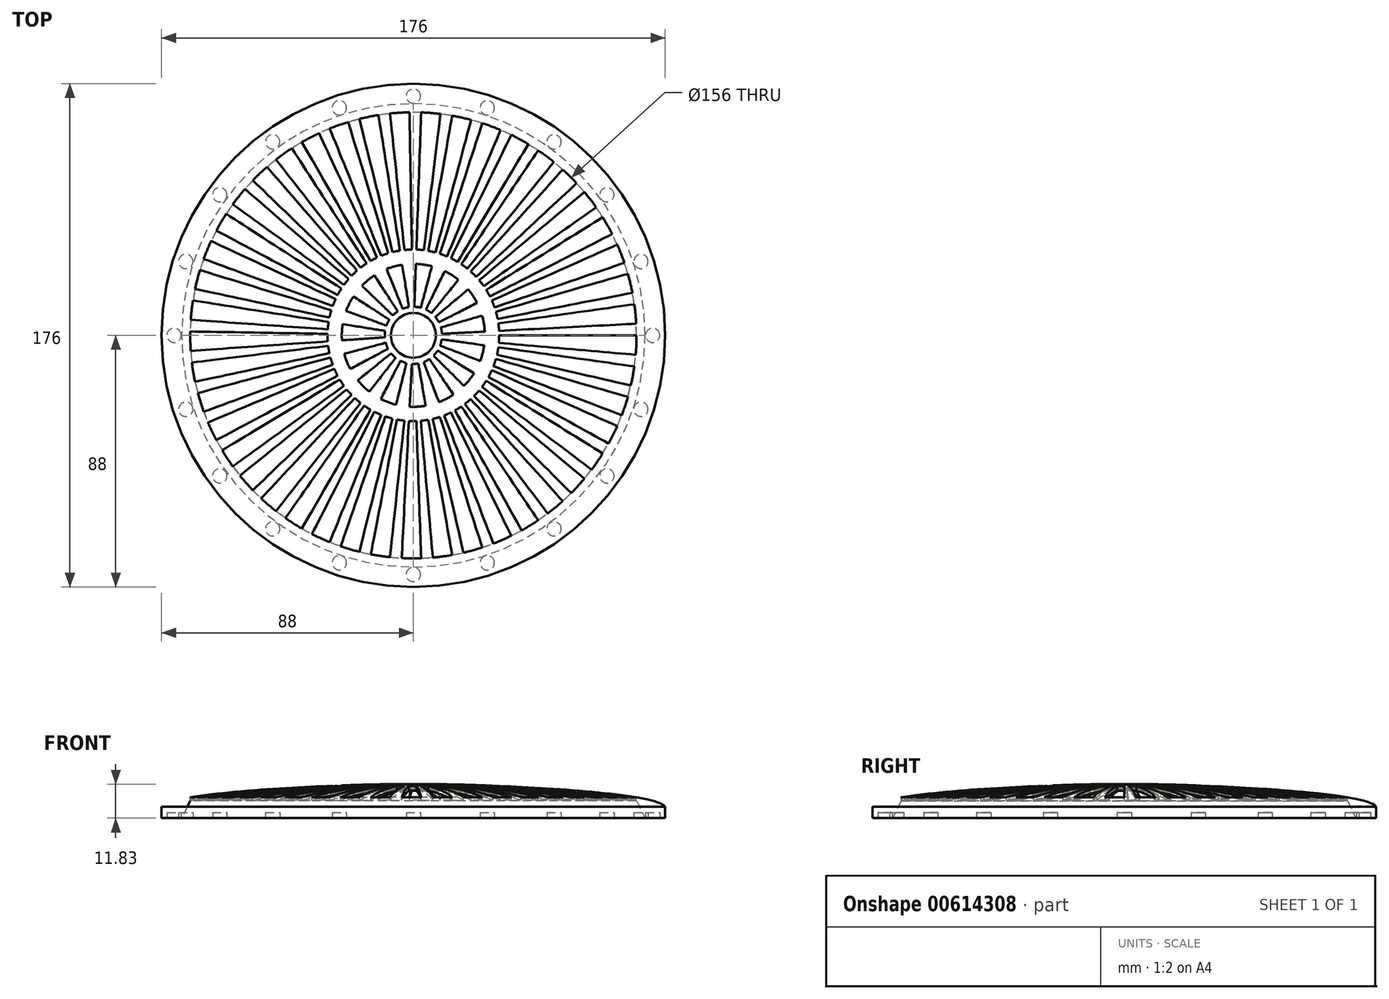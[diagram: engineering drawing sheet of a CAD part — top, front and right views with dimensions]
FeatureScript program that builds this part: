
annotation { "Feature Type Name" : "Feature", "Feature Type Description" : "" }
export const myFeature = defineFeature(function(context is Context, id is Id, definition is map)
    precondition{}
    {
        {
            var Q0;
            Q0=qCreatedBy(makeId("Right.planeOp"),FACE);
            var sketch = newSketch(context, id + "F0", { "sketchPlane" : qUnion([Q0])});
            skLineSegment(sketch, "E0", {"start": v(-78, 0) * mm, "end": v(-88, 0) * mm});
            skLineSegment(sketch, "E1", {"start": v(-88, 0) * mm, "end": v(-88, 4) * mm});
            skLineSegment(sketch, "E2", {"start": v(-88, 4) * mm, "end": v(-78, 4) * mm});
            skLineSegment(sketch, "E3", {"start": v(-78, 4) * mm, "end": v(-78, 0) * mm});
            skFitSpline(sketch, "E4", {"points": [v(-88, 4) * mm, v(-30.6, 11.2) * mm, v(0, 11.8) * mm], "startDerivative": vector(15.82, 21.77) * mm, "endDerivative": vector(56.9, -0.67) * mm});
            skFitSpline(sketch, "E5", {"points": [v(-86, 4) * mm, v(-30.52, 9.57) * mm, v(0, 10.3) * mm], "startDerivative": vector(13.53, 16.7) * mm, "endDerivative": vector(57.66, -2.55) * mm});
            skLineSegment(sketch, "E6", {"start": v(0, 11.8) * mm, "end": v(0, 10.3) * mm});
            skLineSegment(sketch, "E7", {"start": v(-78, 4) * mm, "end": v(-78, 6.25) * mm});
            skSolve(sketch);
        }
        {
            var Q0;
            Q0 = qSketchRegion(id + "F0", true);
            var Q1;
            Q1=sQuery(id+"F0.wireOp",EDGE,"E6");
            revolve(context, id + "F1", {"surfaceOperationType" : NewSurfaceOperationType.NEW, "entities" : qUnion([Q0]), "axis" : qUnion([Q1]), "revolveType" : RevolveType.FULL});
        }
        {
            var Q0;
            Q0=qCreatedBy(makeId("Top.planeOp"),FACE);
            var sketch = newSketch(context, id + "F2", { "sketchPlane" : qUnion([Q0])});
            skArc(sketch, "E8", {"start": v(78, 0) * mm, "mid": v(77.93, -3.4) * mm, "end": v(77.7, -6.8) * mm});
            skLineSegment(sketch, "E9", {"start": v(30, 0) * mm, "end": v(78, 0) * mm});
            skLineSegment(sketch, "E10", {"start": v(29.89, -2.61) * mm, "end": v(77.7, -6.8) * mm});
            skArc(sketch, "E11", {"start": v(30, 0) * mm, "mid": v(29.97, -1.3) * mm, "end": v(29.89, -2.61) * mm});
            skLineSegment(sketch, "E12.1.0", {"start": v(29.96, 1.57) * mm, "end": v(77.9, 4.08) * mm});
            skLineSegment(sketch, "E12.1.1", {"start": v(29.7, 4.18) * mm, "end": v(77.24, 10.86) * mm});
            skArc(sketch, "E12.1.2", {"start": v(77.24, 10.86) * mm, "mid": v(77.64, 7.48) * mm, "end": v(77.9, 4.08) * mm});
            skArc(sketch, "E12.1.3", {"start": v(29.7, 4.18) * mm, "mid": v(29.86, 2.88) * mm, "end": v(29.96, 1.57) * mm});
            skLineSegment(sketch, "E12.2.0", {"start": v(29.45, 5.72) * mm, "end": v(76.57, 14.88) * mm});
            skLineSegment(sketch, "E12.2.1", {"start": v(28.84, 8.27) * mm, "end": v(74.98, 21.5) * mm});
            skArc(sketch, "E12.2.2", {"start": v(74.98, 21.5) * mm, "mid": v(75.84, 18.2) * mm, "end": v(76.57, 14.88) * mm});
            skArc(sketch, "E12.2.3", {"start": v(28.84, 8.27) * mm, "mid": v(29.17, 7) * mm, "end": v(29.45, 5.72) * mm});
            skLineSegment(sketch, "E12.3.0", {"start": v(28.37, 9.77) * mm, "end": v(73.75, 25.4) * mm});
            skLineSegment(sketch, "E12.3.1", {"start": v(27.4, 12.2) * mm, "end": v(71.26, 31.73) * mm});
            skArc(sketch, "E12.3.2", {"start": v(71.26, 31.73) * mm, "mid": v(72.57, 28.59) * mm, "end": v(73.75, 25.4) * mm});
            skArc(sketch, "E12.3.3", {"start": v(27.4, 12.2) * mm, "mid": v(27.91, 11) * mm, "end": v(28.37, 9.77) * mm});
            skLineSegment(sketch, "E12.4.0", {"start": v(26.73, 13.62) * mm, "end": v(69.5, 35.41) * mm});
            skLineSegment(sketch, "E12.4.1", {"start": v(25.44, 15.9) * mm, "end": v(66.15, 41.33) * mm});
            skArc(sketch, "E12.4.2", {"start": v(66.15, 41.33) * mm, "mid": v(67.89, 38.4) * mm, "end": v(69.5, 35.41) * mm});
            skArc(sketch, "E12.4.3", {"start": v(25.44, 15.9) * mm, "mid": v(26.11, 14.77) * mm, "end": v(26.73, 13.62) * mm});
            skLineSegment(sketch, "E12.5.0", {"start": v(24.57, 17.2) * mm, "end": v(63.9, 44.74) * mm});
            skLineSegment(sketch, "E12.5.1", {"start": v(22.98, 19.28) * mm, "end": v(59.75, 50.14) * mm});
            skArc(sketch, "E12.5.2", {"start": v(59.75, 50.14) * mm, "mid": v(61.88, 47.48) * mm, "end": v(63.9, 44.74) * mm});
            skArc(sketch, "E12.5.3", {"start": v(22.98, 19.28) * mm, "mid": v(23.8, 18.26) * mm, "end": v(24.57, 17.2) * mm});
            skLineSegment(sketch, "E12.6.0", {"start": v(21.94, 20.46) * mm, "end": v(57.05, 53.2) * mm});
            skLineSegment(sketch, "E12.6.1", {"start": v(20.07, 22.3) * mm, "end": v(52.2, 57.97) * mm});
            skArc(sketch, "E12.6.2", {"start": v(52.2, 57.97) * mm, "mid": v(54.67, 55.63) * mm, "end": v(57.05, 53.2) * mm});
            skArc(sketch, "E12.6.3", {"start": v(20.07, 22.3) * mm, "mid": v(21.03, 21.4) * mm, "end": v(21.94, 20.46) * mm});
            skLineSegment(sketch, "E12.7.0", {"start": v(18.88, 23.31) * mm, "end": v(49.09, 60.62) * mm});
            skLineSegment(sketch, "E12.7.1", {"start": v(16.78, 24.87) * mm, "end": v(43.62, 64.66) * mm});
            skArc(sketch, "E12.7.2", {"start": v(43.62, 64.66) * mm, "mid": v(46.4, 62.7) * mm, "end": v(49.09, 60.62) * mm});
            skArc(sketch, "E12.7.3", {"start": v(16.78, 24.87) * mm, "mid": v(17.84, 24.12) * mm, "end": v(18.88, 23.31) * mm});
            skLineSegment(sketch, "E12.8.0", {"start": v(15.45, 25.72) * mm, "end": v(40.17, 66.86) * mm});
            skLineSegment(sketch, "E12.8.1", {"start": v(13.15, 26.96) * mm, "end": v(34.2, 70.1) * mm});
            skArc(sketch, "E12.8.2", {"start": v(34.2, 70.1) * mm, "mid": v(37.22, 68.55) * mm, "end": v(40.17, 66.86) * mm});
            skArc(sketch, "E12.8.3", {"start": v(13.15, 26.96) * mm, "mid": v(14.31, 26.36) * mm, "end": v(15.45, 25.72) * mm});
            skLineSegment(sketch, "E12.9.0", {"start": v(11.72, 27.62) * mm, "end": v(30.48, 71.8) * mm});
            skLineSegment(sketch, "E12.9.1", {"start": v(9.27, 28.53) * mm, "end": v(24.1, 74.18) * mm});
            skArc(sketch, "E12.9.2", {"start": v(24.1, 74.18) * mm, "mid": v(27.32, 73.06) * mm, "end": v(30.48, 71.8) * mm});
            skArc(sketch, "E12.9.3", {"start": v(9.27, 28.53) * mm, "mid": v(10.5, 28.1) * mm, "end": v(11.72, 27.62) * mm});
            skLineSegment(sketch, "E12.10.0", {"start": v(7.76, 28.98) * mm, "end": v(20.19, 75.34) * mm});
            skLineSegment(sketch, "E12.10.1", {"start": v(5.2, 29.54) * mm, "end": v(13.54, 76.82) * mm});
            skArc(sketch, "E12.10.2", {"start": v(13.54, 76.82) * mm, "mid": v(16.88, 76.15) * mm, "end": v(20.19, 75.34) * mm});
            skArc(sketch, "E12.10.3", {"start": v(5.2, 29.54) * mm, "mid": v(6.5, 29.29) * mm, "end": v(7.76, 28.98) * mm});
            skLineSegment(sketch, "E12.11.0", {"start": v(3.66, 29.78) * mm, "end": v(9.5, 77.42) * mm});
            skLineSegment(sketch, "E12.11.1", {"start": v(1.05, 29.98) * mm, "end": v(2.72, 77.95) * mm});
            skArc(sketch, "E12.11.2", {"start": v(2.72, 77.95) * mm, "mid": v(6.12, 77.76) * mm, "end": v(9.5, 77.42) * mm});
            skArc(sketch, "E12.11.3", {"start": v(1.05, 29.98) * mm, "mid": v(2.35, 29.9) * mm, "end": v(3.66, 29.78) * mm});
            skLineSegment(sketch, "E12.12.0", {"start": v(-0.52, 30) * mm, "end": v(-1.36, 77.99) * mm});
            skLineSegment(sketch, "E12.12.1", {"start": v(-3.14, 29.84) * mm, "end": v(-8.15, 77.57) * mm});
            skArc(sketch, "E12.12.2", {"start": v(-8.15, 77.57) * mm, "mid": v(-4.76, 77.85) * mm, "end": v(-1.36, 77.99) * mm});
            skArc(sketch, "E12.12.3", {"start": v(-3.14, 29.84) * mm, "mid": v(-1.83, 29.94) * mm, "end": v(-0.52, 30) * mm});
            skLineSegment(sketch, "E12.13.0", {"start": v(-4.7, 29.63) * mm, "end": v(-12.2, 77.04) * mm});
            skLineSegment(sketch, "E12.13.1", {"start": v(-7.26, 29.1) * mm, "end": v(-18.87, 75.68) * mm});
            skArc(sketch, "E12.13.2", {"start": v(-18.87, 75.68) * mm, "mid": v(-15.55, 76.43) * mm, "end": v(-12.2, 77.04) * mm});
            skArc(sketch, "E12.13.3", {"start": v(-7.26, 29.1) * mm, "mid": v(-5.98, 29.4) * mm, "end": v(-4.7, 29.63) * mm});
            skLineSegment(sketch, "E12.14.0", {"start": v(-8.77, 28.69) * mm, "end": v(-22.8, 74.6) * mm});
            skLineSegment(sketch, "E12.14.1", {"start": v(-11.24, 27.82) * mm, "end": v(-29.22, 72.32) * mm});
            skArc(sketch, "E12.14.2", {"start": v(-29.22, 72.32) * mm, "mid": v(-26.04, 73.53) * mm, "end": v(-22.8, 74.6) * mm});
            skArc(sketch, "E12.14.3", {"start": v(-11.24, 27.82) * mm, "mid": v(-10.01, 28.28) * mm, "end": v(-8.77, 28.69) * mm});
            skLineSegment(sketch, "E12.15.0", {"start": v(-12.68, 27.19) * mm, "end": v(-32.96, 70.7) * mm});
            skLineSegment(sketch, "E12.15.1", {"start": v(-15, 25.98) * mm, "end": v(-39, 67.55) * mm});
            skArc(sketch, "E12.15.2", {"start": v(-39, 67.55) * mm, "mid": v(-36.02, 69.19) * mm, "end": v(-32.96, 70.7) * mm});
            skArc(sketch, "E12.15.3", {"start": v(-15, 25.98) * mm, "mid": v(-13.85, 26.61) * mm, "end": v(-12.68, 27.19) * mm});
            skLineSegment(sketch, "E12.16.0", {"start": v(-16.34, 25.16) * mm, "end": v(-42.48, 65.42) * mm});
            skLineSegment(sketch, "E12.16.1", {"start": v(-18.47, 23.64) * mm, "end": v(-48.02, 61.46) * mm});
            skArc(sketch, "E12.16.2", {"start": v(-48.02, 61.46) * mm, "mid": v(-45.3, 63.5) * mm, "end": v(-42.48, 65.42) * mm});
            skArc(sketch, "E12.16.3", {"start": v(-18.47, 23.64) * mm, "mid": v(-17.42, 24.42) * mm, "end": v(-16.34, 25.16) * mm});
            skLineSegment(sketch, "E12.17.0", {"start": v(-19.68, 22.64) * mm, "end": v(-51.17, 58.87) * mm});
            skLineSegment(sketch, "E12.17.1", {"start": v(-21.58, 20.84) * mm, "end": v(-56.1, 54.18) * mm});
            skArc(sketch, "E12.17.2", {"start": v(-56.1, 54.18) * mm, "mid": v(-53.7, 56.58) * mm, "end": v(-51.17, 58.87) * mm});
            skArc(sketch, "E12.17.3", {"start": v(-21.58, 20.84) * mm, "mid": v(-20.65, 21.76) * mm, "end": v(-19.68, 22.64) * mm});
            skLineSegment(sketch, "E12.18.0", {"start": v(-22.64, 19.68) * mm, "end": v(-58.87, 51.17) * mm});
            skLineSegment(sketch, "E12.18.1", {"start": v(-24.27, 17.63) * mm, "end": v(-63.1, 45.85) * mm});
            skArc(sketch, "E12.18.2", {"start": v(-63.1, 45.85) * mm, "mid": v(-61.04, 48.56) * mm, "end": v(-58.87, 51.17) * mm});
            skArc(sketch, "E12.18.3", {"start": v(-24.27, 17.63) * mm, "mid": v(-23.48, 18.68) * mm, "end": v(-22.64, 19.68) * mm});
            skLineSegment(sketch, "E12.19.0", {"start": v(-25.16, 16.34) * mm, "end": v(-65.42, 42.48) * mm});
            skLineSegment(sketch, "E12.19.1", {"start": v(-26.49, 14.08) * mm, "end": v(-68.87, 36.62) * mm});
            skArc(sketch, "E12.19.2", {"start": v(-68.87, 36.62) * mm, "mid": v(-67.2, 39.59) * mm, "end": v(-65.42, 42.48) * mm});
            skArc(sketch, "E12.19.3", {"start": v(-26.49, 14.08) * mm, "mid": v(-25.85, 15.23) * mm, "end": v(-25.16, 16.34) * mm});
            skLineSegment(sketch, "E12.20.0", {"start": v(-27.19, 12.68) * mm, "end": v(-70.7, 32.96) * mm});
            skLineSegment(sketch, "E12.20.1", {"start": v(-28.2, 10.26) * mm, "end": v(-73.3, 26.68) * mm});
            skArc(sketch, "E12.20.2", {"start": v(-73.3, 26.68) * mm, "mid": v(-72.06, 29.85) * mm, "end": v(-70.7, 32.96) * mm});
            skArc(sketch, "E12.20.3", {"start": v(-28.2, 10.26) * mm, "mid": v(-27.72, 11.48) * mm, "end": v(-27.19, 12.68) * mm});
            skLineSegment(sketch, "E12.21.0", {"start": v(-28.69, 8.77) * mm, "end": v(-74.6, 22.8) * mm});
            skLineSegment(sketch, "E12.21.1", {"start": v(-29.34, 6.24) * mm, "end": v(-76.3, 16.22) * mm});
            skArc(sketch, "E12.21.2", {"start": v(-76.3, 16.22) * mm, "mid": v(-75.52, 19.53) * mm, "end": v(-74.6, 22.8) * mm});
            skArc(sketch, "E12.21.3", {"start": v(-29.34, 6.24) * mm, "mid": v(-29.04, 7.51) * mm, "end": v(-28.69, 8.77) * mm});
            skLineSegment(sketch, "E12.22.0", {"start": v(-29.63, 4.7) * mm, "end": v(-77.04, 12.2) * mm});
            skLineSegment(sketch, "E12.22.1", {"start": v(-29.93, 2.1) * mm, "end": v(-77.8, 5.44) * mm});
            skArc(sketch, "E12.22.2", {"start": v(-77.8, 5.44) * mm, "mid": v(-77.5, 8.83) * mm, "end": v(-77.04, 12.2) * mm});
            skArc(sketch, "E12.22.3", {"start": v(-29.93, 2.1) * mm, "mid": v(-29.8, 3.4) * mm, "end": v(-29.63, 4.7) * mm});
            skLineSegment(sketch, "E12.23.0", {"start": v(-30, 0.52) * mm, "end": v(-77.99, 1.36) * mm});
            skLineSegment(sketch, "E12.23.1", {"start": v(-29.93, -2.1) * mm, "end": v(-77.8, -5.44) * mm});
            skArc(sketch, "E12.23.2", {"start": v(-77.8, -5.44) * mm, "mid": v(-77.97, -2.04) * mm, "end": v(-77.99, 1.36) * mm});
            skArc(sketch, "E12.23.3", {"start": v(-29.93, -2.1) * mm, "mid": v(-29.99, -0.79) * mm, "end": v(-30, 0.52) * mm});
            skLineSegment(sketch, "E12.24.0", {"start": v(-29.78, -3.66) * mm, "end": v(-77.42, -9.5) * mm});
            skLineSegment(sketch, "E12.24.1", {"start": v(-29.34, -6.24) * mm, "end": v(-76.3, -16.22) * mm});
            skArc(sketch, "E12.24.2", {"start": v(-76.3, -16.22) * mm, "mid": v(-76.93, -12.87) * mm, "end": v(-77.42, -9.5) * mm});
            skArc(sketch, "E12.24.3", {"start": v(-29.34, -6.24) * mm, "mid": v(-29.59, -4.95) * mm, "end": v(-29.78, -3.66) * mm});
            skLineSegment(sketch, "E12.25.0", {"start": v(-28.98, -7.76) * mm, "end": v(-75.34, -20.19) * mm});
            skLineSegment(sketch, "E12.25.1", {"start": v(-28.2, -10.26) * mm, "end": v(-73.3, -26.68) * mm});
            skArc(sketch, "E12.25.2", {"start": v(-73.3, -26.68) * mm, "mid": v(-74.39, -23.46) * mm, "end": v(-75.34, -20.19) * mm});
            skArc(sketch, "E12.25.3", {"start": v(-28.2, -10.26) * mm, "mid": v(-28.61, -9.02) * mm, "end": v(-28.98, -7.76) * mm});
            skLineSegment(sketch, "E12.26.0", {"start": v(-27.62, -11.72) * mm, "end": v(-71.8, -30.48) * mm});
            skLineSegment(sketch, "E12.26.1", {"start": v(-26.49, -14.08) * mm, "end": v(-68.87, -36.62) * mm});
            skArc(sketch, "E12.26.2", {"start": v(-68.87, -36.62) * mm, "mid": v(-70.4, -33.58) * mm, "end": v(-71.8, -30.48) * mm});
            skArc(sketch, "E12.26.3", {"start": v(-26.49, -14.08) * mm, "mid": v(-27.08, -12.92) * mm, "end": v(-27.62, -11.72) * mm});
            skLineSegment(sketch, "E12.27.0", {"start": v(-25.72, -15.45) * mm, "end": v(-66.86, -40.17) * mm});
            skLineSegment(sketch, "E12.27.1", {"start": v(-24.27, -17.63) * mm, "end": v(-63.1, -45.85) * mm});
            skArc(sketch, "E12.27.2", {"start": v(-63.1, -45.85) * mm, "mid": v(-65.04, -43.05) * mm, "end": v(-66.86, -40.17) * mm});
            skArc(sketch, "E12.27.3", {"start": v(-24.27, -17.63) * mm, "mid": v(-25.02, -16.56) * mm, "end": v(-25.72, -15.45) * mm});
            skLineSegment(sketch, "E12.28.0", {"start": v(-23.31, -18.88) * mm, "end": v(-60.62, -49.09) * mm});
            skLineSegment(sketch, "E12.28.1", {"start": v(-21.58, -20.84) * mm, "end": v(-56.1, -54.18) * mm});
            skArc(sketch, "E12.28.2", {"start": v(-56.1, -54.18) * mm, "mid": v(-58.42, -51.68) * mm, "end": v(-60.62, -49.09) * mm});
            skArc(sketch, "E12.28.3", {"start": v(-21.58, -20.84) * mm, "mid": v(-22.47, -19.88) * mm, "end": v(-23.31, -18.88) * mm});
            skLineSegment(sketch, "E12.29.0", {"start": v(-20.46, -21.94) * mm, "end": v(-53.2, -57.05) * mm});
            skLineSegment(sketch, "E12.29.1", {"start": v(-18.47, -23.64) * mm, "end": v(-48.02, -61.46) * mm});
            skArc(sketch, "E12.29.2", {"start": v(-48.02, -61.46) * mm, "mid": v(-50.66, -59.31) * mm, "end": v(-53.2, -57.05) * mm});
            skArc(sketch, "E12.29.3", {"start": v(-18.47, -23.64) * mm, "mid": v(-19.48, -22.81) * mm, "end": v(-20.46, -21.94) * mm});
            skLineSegment(sketch, "E13.1.30.0", {"start": v(-17.2, -24.57) * mm, "end": v(-44.74, -63.9) * mm});
            skLineSegment(sketch, "E13.3.30.0", {"start": v(-15, -25.98) * mm, "end": v(-39, -67.55) * mm});
            skArc(sketch, "E13.6.30.0", {"start": v(-39, -67.55) * mm, "mid": v(-41.9, -65.78) * mm, "end": v(-44.74, -63.9) * mm});
            skArc(sketch, "E13.10.30.0", {"start": v(-15, -25.98) * mm, "mid": v(-16.12, -25.3) * mm, "end": v(-17.2, -24.57) * mm});
            skLineSegment(sketch, "E13.1.31.0", {"start": v(-13.62, -26.73) * mm, "end": v(-35.41, -69.5) * mm});
            skLineSegment(sketch, "E13.3.31.0", {"start": v(-11.24, -27.82) * mm, "end": v(-29.22, -72.32) * mm});
            skArc(sketch, "E13.6.31.0", {"start": v(-29.22, -72.32) * mm, "mid": v(-32.35, -70.98) * mm, "end": v(-35.41, -69.5) * mm});
            skArc(sketch, "E13.10.31.0", {"start": v(-11.24, -27.82) * mm, "mid": v(-12.44, -27.3) * mm, "end": v(-13.62, -26.73) * mm});
            skLineSegment(sketch, "E13.1.32.0", {"start": v(-9.77, -28.37) * mm, "end": v(-25.4, -73.75) * mm});
            skLineSegment(sketch, "E13.3.32.0", {"start": v(-7.26, -29.1) * mm, "end": v(-18.87, -75.68) * mm});
            skArc(sketch, "E13.6.32.0", {"start": v(-18.87, -75.68) * mm, "mid": v(-22.15, -74.79) * mm, "end": v(-25.4, -73.75) * mm});
            skArc(sketch, "E13.10.32.0", {"start": v(-7.26, -29.1) * mm, "mid": v(-8.52, -28.76) * mm, "end": v(-9.77, -28.37) * mm});
            skLineSegment(sketch, "E13.1.33.0", {"start": v(-5.72, -29.45) * mm, "end": v(-14.88, -76.57) * mm});
            skLineSegment(sketch, "E13.3.33.0", {"start": v(-3.14, -29.84) * mm, "end": v(-8.15, -77.57) * mm});
            skArc(sketch, "E13.6.33.0", {"start": v(-8.15, -77.57) * mm, "mid": v(-11.53, -77.14) * mm, "end": v(-14.88, -76.57) * mm});
            skArc(sketch, "E13.10.33.0", {"start": v(-3.14, -29.84) * mm, "mid": v(-4.43, -29.67) * mm, "end": v(-5.72, -29.45) * mm});
            skLineSegment(sketch, "E13.1.34.0", {"start": v(-1.57, -29.96) * mm, "end": v(-4.08, -77.9) * mm});
            skLineSegment(sketch, "E13.3.34.0", {"start": v(1.05, -29.98) * mm, "end": v(2.72, -77.95) * mm});
            skArc(sketch, "E13.6.34.0", {"start": v(2.72, -77.95) * mm, "mid": v(-0.68, -78) * mm, "end": v(-4.08, -77.9) * mm});
            skArc(sketch, "E13.10.34.0", {"start": v(1.05, -29.98) * mm, "mid": v(-0.26, -30) * mm, "end": v(-1.57, -29.96) * mm});
            skLineSegment(sketch, "E13.1.35.0", {"start": v(2.61, -29.89) * mm, "end": v(6.8, -77.7) * mm});
            skLineSegment(sketch, "E13.3.35.0", {"start": v(5.2, -29.54) * mm, "end": v(13.54, -76.82) * mm});
            skArc(sketch, "E13.6.35.0", {"start": v(13.54, -76.82) * mm, "mid": v(10.18, -77.33) * mm, "end": v(6.8, -77.7) * mm});
            skArc(sketch, "E13.10.35.0", {"start": v(5.2, -29.54) * mm, "mid": v(3.92, -29.74) * mm, "end": v(2.61, -29.89) * mm});
            skLineSegment(sketch, "E13.1.36.0", {"start": v(6.75, -29.23) * mm, "end": v(17.55, -76) * mm});
            skLineSegment(sketch, "E13.3.36.0", {"start": v(9.27, -28.53) * mm, "end": v(24.1, -74.18) * mm});
            skArc(sketch, "E13.6.36.0", {"start": v(24.1, -74.18) * mm, "mid": v(20.84, -75.16) * mm, "end": v(17.55, -76) * mm});
            skArc(sketch, "E13.10.36.0", {"start": v(9.27, -28.53) * mm, "mid": v(8.02, -28.9) * mm, "end": v(6.75, -29.23) * mm});
            skLineSegment(sketch, "E13.1.37.0", {"start": v(10.75, -28) * mm, "end": v(27.95, -72.82) * mm});
            skLineSegment(sketch, "E13.3.37.0", {"start": v(13.15, -26.96) * mm, "end": v(34.2, -70.1) * mm});
            skArc(sketch, "E13.6.37.0", {"start": v(34.2, -70.1) * mm, "mid": v(31.1, -71.53) * mm, "end": v(27.95, -72.82) * mm});
            skArc(sketch, "E13.10.37.0", {"start": v(13.15, -26.96) * mm, "mid": v(11.96, -27.51) * mm, "end": v(10.75, -28) * mm});
            skLineSegment(sketch, "E13.1.38.0", {"start": v(14.54, -26.24) * mm, "end": v(37.82, -68.22) * mm});
            skLineSegment(sketch, "E13.3.38.0", {"start": v(16.78, -24.87) * mm, "end": v(43.62, -64.66) * mm});
            skArc(sketch, "E13.6.38.0", {"start": v(43.62, -64.66) * mm, "mid": v(40.75, -66.5) * mm, "end": v(37.82, -68.22) * mm});
            skArc(sketch, "E13.10.38.0", {"start": v(16.78, -24.87) * mm, "mid": v(15.67, -25.58) * mm, "end": v(14.54, -26.24) * mm});
            skLineSegment(sketch, "E13.1.39.0", {"start": v(18.05, -23.96) * mm, "end": v(46.94, -62.3) * mm});
            skLineSegment(sketch, "E13.3.39.0", {"start": v(20.07, -22.3) * mm, "end": v(52.2, -57.97) * mm});
            skArc(sketch, "E13.6.39.0", {"start": v(52.2, -57.97) * mm, "mid": v(49.61, -60.19) * mm, "end": v(46.94, -62.3) * mm});
            skArc(sketch, "E13.10.39.0", {"start": v(20.07, -22.3) * mm, "mid": v(19.08, -23.15) * mm, "end": v(18.05, -23.96) * mm});
            skLineSegment(sketch, "E13.1.40.0", {"start": v(21.21, -21.21) * mm, "end": v(55.15, -55.15) * mm});
            skLineSegment(sketch, "E13.3.40.0", {"start": v(22.98, -19.28) * mm, "end": v(59.75, -50.14) * mm});
            skArc(sketch, "E13.6.40.0", {"start": v(59.75, -50.14) * mm, "mid": v(57.5, -52.7) * mm, "end": v(55.15, -55.15) * mm});
            skArc(sketch, "E13.10.40.0", {"start": v(22.98, -19.28) * mm, "mid": v(22.12, -20.27) * mm, "end": v(21.21, -21.21) * mm});
            skLineSegment(sketch, "E13.1.41.0", {"start": v(23.96, -18.05) * mm, "end": v(62.3, -46.94) * mm});
            skLineSegment(sketch, "E13.3.41.0", {"start": v(25.44, -15.9) * mm, "end": v(66.15, -41.33) * mm});
            skArc(sketch, "E13.6.41.0", {"start": v(66.15, -41.33) * mm, "mid": v(64.28, -44.18) * mm, "end": v(62.3, -46.94) * mm});
            skArc(sketch, "E13.10.41.0", {"start": v(25.44, -15.9) * mm, "mid": v(24.72, -17) * mm, "end": v(23.96, -18.05) * mm});
            skLineSegment(sketch, "E13.1.42.0", {"start": v(26.24, -14.54) * mm, "end": v(68.22, -37.82) * mm});
            skLineSegment(sketch, "E13.3.42.0", {"start": v(27.4, -12.2) * mm, "end": v(71.26, -31.73) * mm});
            skArc(sketch, "E13.6.42.0", {"start": v(71.26, -31.73) * mm, "mid": v(69.8, -34.8) * mm, "end": v(68.22, -37.82) * mm});
            skArc(sketch, "E13.10.42.0", {"start": v(27.4, -12.2) * mm, "mid": v(26.85, -13.39) * mm, "end": v(26.24, -14.54) * mm});
            skLineSegment(sketch, "E13.1.43.0", {"start": v(28, -10.75) * mm, "end": v(72.82, -27.95) * mm});
            skLineSegment(sketch, "E13.3.43.0", {"start": v(28.84, -8.27) * mm, "end": v(74.98, -21.5) * mm});
            skArc(sketch, "E13.6.43.0", {"start": v(74.98, -21.5) * mm, "mid": v(73.97, -24.75) * mm, "end": v(72.82, -27.95) * mm});
            skArc(sketch, "E13.10.43.0", {"start": v(28.84, -8.27) * mm, "mid": v(28.45, -9.52) * mm, "end": v(28, -10.75) * mm});
            skLineSegment(sketch, "E13.1.44.0", {"start": v(29.23, -6.75) * mm, "end": v(76, -17.55) * mm});
            skLineSegment(sketch, "E13.3.44.0", {"start": v(29.7, -4.18) * mm, "end": v(77.24, -10.86) * mm});
            skArc(sketch, "E13.6.44.0", {"start": v(77.24, -10.86) * mm, "mid": v(76.7, -14.21) * mm, "end": v(76, -17.55) * mm});
            skArc(sketch, "E13.10.44.0", {"start": v(29.7, -4.18) * mm, "mid": v(29.5, -5.47) * mm, "end": v(29.23, -6.75) * mm});
            skArc(sketch, "E14", {"start": v(-24.7, 3.91) * mm, "mid": v(-24.98, 1.1) * mm, "end": v(-24.94, -1.74) * mm});
            skLineSegment(sketch, "E15", {"start": v(-9.88, 1.56) * mm, "end": v(-24.7, 3.91) * mm});
            skLineSegment(sketch, "E16", {"start": v(-9.98, -0.7) * mm, "end": v(-24.94, -1.74) * mm});
            skCircle(sketch, "E17", {"center": v(0, 0) * mm, "radius": 7.85 * mm});
            skArc(sketch, "E18", {"start": v(-9.98, -0.7) * mm, "mid": v(-10, 0.44) * mm, "end": v(-9.88, 1.56) * mm});
            skLineSegment(sketch, "E19.1.0", {"start": v(-9.66, -2.59) * mm, "end": v(-24.15, -6.47) * mm});
            skArc(sketch, "E19.1.1", {"start": v(-24.15, -6.47) * mm, "mid": v(-23.26, -9.16) * mm, "end": v(-22.07, -11.74) * mm});
            skLineSegment(sketch, "E19.1.2", {"start": v(-8.83, -4.7) * mm, "end": v(-22.07, -11.74) * mm});
            skArc(sketch, "E19.1.3", {"start": v(-8.83, -4.7) * mm, "mid": v(-9.3, -3.67) * mm, "end": v(-9.66, -2.59) * mm});
            skLineSegment(sketch, "E19.2.0", {"start": v(-7.77, -6.3) * mm, "end": v(-19.43, -15.73) * mm});
            skArc(sketch, "E19.2.1", {"start": v(-19.43, -15.73) * mm, "mid": v(-17.52, -17.83) * mm, "end": v(-15.4, -19.7) * mm});
            skLineSegment(sketch, "E19.2.2", {"start": v(-6.16, -7.88) * mm, "end": v(-15.4, -19.7) * mm});
            skArc(sketch, "E19.2.3", {"start": v(-6.16, -7.88) * mm, "mid": v(-7, -7.13) * mm, "end": v(-7.77, -6.3) * mm});
            skLineSegment(sketch, "E19.3.0", {"start": v(-4.54, -8.91) * mm, "end": v(-11.35, -22.28) * mm});
            skArc(sketch, "E19.3.1", {"start": v(-11.35, -22.28) * mm, "mid": v(-8.76, -23.42) * mm, "end": v(-6.05, -24.26) * mm});
            skLineSegment(sketch, "E19.3.2", {"start": v(-2.42, -9.7) * mm, "end": v(-6.05, -24.26) * mm});
            skArc(sketch, "E19.3.3", {"start": v(-2.42, -9.7) * mm, "mid": v(-3.5, -9.37) * mm, "end": v(-4.54, -8.91) * mm});
            skLineSegment(sketch, "E19.4.0", {"start": v(-0.52, -9.99) * mm, "end": v(-1.3, -24.97) * mm});
            skArc(sketch, "E19.4.1", {"start": v(-1.3, -24.97) * mm, "mid": v(1.53, -24.95) * mm, "end": v(4.34, -24.62) * mm});
            skLineSegment(sketch, "E19.4.2", {"start": v(1.74, -9.85) * mm, "end": v(4.34, -24.62) * mm});
            skArc(sketch, "E19.4.3", {"start": v(1.74, -9.85) * mm, "mid": v(0.61, -9.98) * mm, "end": v(-0.52, -9.99) * mm});
            skLineSegment(sketch, "E19.5.0", {"start": v(3.58, -9.34) * mm, "end": v(8.96, -23.34) * mm});
            skArc(sketch, "E19.5.1", {"start": v(8.96, -23.34) * mm, "mid": v(11.54, -22.18) * mm, "end": v(13.98, -20.73) * mm});
            skLineSegment(sketch, "E19.5.2", {"start": v(5.6, -8.3) * mm, "end": v(13.98, -20.73) * mm});
            skArc(sketch, "E19.5.3", {"start": v(5.6, -8.3) * mm, "mid": v(4.62, -8.87) * mm, "end": v(3.58, -9.34) * mm});
            skLineSegment(sketch, "E19.6.0", {"start": v(7.07, -7.07) * mm, "end": v(17.68, -17.68) * mm});
            skArc(sketch, "E19.6.1", {"start": v(17.68, -17.68) * mm, "mid": v(19.57, -15.56) * mm, "end": v(21.2, -13.25) * mm});
            skLineSegment(sketch, "E19.6.2", {"start": v(8.48, -5.3) * mm, "end": v(21.2, -13.25) * mm});
            skArc(sketch, "E19.6.3", {"start": v(8.48, -5.3) * mm, "mid": v(7.83, -6.23) * mm, "end": v(7.07, -7.07) * mm});
            skLineSegment(sketch, "E19.7.0", {"start": v(9.34, -3.58) * mm, "end": v(23.34, -8.96) * mm});
            skArc(sketch, "E19.7.1", {"start": v(23.34, -8.96) * mm, "mid": v(24.2, -6.26) * mm, "end": v(24.76, -3.48) * mm});
            skLineSegment(sketch, "E19.7.2", {"start": v(9.9, -1.4) * mm, "end": v(24.76, -3.48) * mm});
            skArc(sketch, "E19.7.3", {"start": v(9.9, -1.4) * mm, "mid": v(9.68, -2.5) * mm, "end": v(9.34, -3.58) * mm});
            skLineSegment(sketch, "E19.8.0", {"start": v(9.99, 0.52) * mm, "end": v(24.97, 1.3) * mm});
            skArc(sketch, "E19.8.1", {"start": v(24.97, 1.3) * mm, "mid": v(24.66, 4.13) * mm, "end": v(24.03, 6.9) * mm});
            skLineSegment(sketch, "E19.8.2", {"start": v(9.61, 2.76) * mm, "end": v(24.03, 6.9) * mm});
            skArc(sketch, "E19.8.3", {"start": v(9.61, 2.76) * mm, "mid": v(9.86, 1.65) * mm, "end": v(9.99, 0.52) * mm});
            skLineSegment(sketch, "E19.9.0", {"start": v(8.91, 4.54) * mm, "end": v(22.28, 11.35) * mm});
            skArc(sketch, "E19.9.1", {"start": v(22.28, 11.35) * mm, "mid": v(20.85, 13.8) * mm, "end": v(19.15, 16.07) * mm});
            skLineSegment(sketch, "E19.9.2", {"start": v(7.66, 6.43) * mm, "end": v(19.15, 16.07) * mm});
            skArc(sketch, "E19.9.3", {"start": v(7.66, 6.43) * mm, "mid": v(8.34, 5.52) * mm, "end": v(8.91, 4.54) * mm});
            skLineSegment(sketch, "E19.10.0", {"start": v(6.3, 7.77) * mm, "end": v(15.73, 19.43) * mm});
            skArc(sketch, "E19.10.1", {"start": v(15.73, 19.43) * mm, "mid": v(13.43, 21.08) * mm, "end": v(10.96, 22.47) * mm});
            skLineSegment(sketch, "E19.10.2", {"start": v(4.38, 8.99) * mm, "end": v(10.96, 22.47) * mm});
            skArc(sketch, "E19.10.3", {"start": v(4.38, 8.99) * mm, "mid": v(5.37, 8.43) * mm, "end": v(6.3, 7.77) * mm});
            skLineSegment(sketch, "E19.11.0", {"start": v(2.59, 9.66) * mm, "end": v(6.47, 24.15) * mm});
            skArc(sketch, "E19.11.1", {"start": v(6.47, 24.15) * mm, "mid": v(3.7, 24.73) * mm, "end": v(0.87, 24.98) * mm});
            skLineSegment(sketch, "E19.11.2", {"start": v(0.35, 10) * mm, "end": v(0.87, 24.98) * mm});
            skArc(sketch, "E19.11.3", {"start": v(0.35, 10) * mm, "mid": v(1.48, 9.9) * mm, "end": v(2.59, 9.66) * mm});
            skLineSegment(sketch, "E19.12.0", {"start": v(-1.56, 9.88) * mm, "end": v(-3.91, 24.7) * mm});
            skArc(sketch, "E19.12.1", {"start": v(-3.91, 24.7) * mm, "mid": v(-6.68, 24.1) * mm, "end": v(-9.37, 23.18) * mm});
            skLineSegment(sketch, "E19.12.2", {"start": v(-3.75, 9.27) * mm, "end": v(-9.37, 23.18) * mm});
            skArc(sketch, "E19.12.3", {"start": v(-3.75, 9.27) * mm, "mid": v(-2.67, 9.64) * mm, "end": v(-1.56, 9.88) * mm});
            skLineSegment(sketch, "E19.13.0", {"start": v(-5.45, 8.39) * mm, "end": v(-13.62, 20.97) * mm});
            skArc(sketch, "E19.13.1", {"start": v(-13.62, 20.97) * mm, "mid": v(-15.9, 19.3) * mm, "end": v(-17.98, 17.37) * mm});
            skLineSegment(sketch, "E19.13.2", {"start": v(-7.2, 6.95) * mm, "end": v(-17.98, 17.37) * mm});
            skArc(sketch, "E19.13.3", {"start": v(-7.2, 6.95) * mm, "mid": v(-6.36, 7.72) * mm, "end": v(-5.45, 8.39) * mm});
            skLineSegment(sketch, "E19.14.0", {"start": v(-8.39, 5.45) * mm, "end": v(-20.97, 13.62) * mm});
            skArc(sketch, "E19.14.1", {"start": v(-20.97, 13.62) * mm, "mid": v(-22.37, 11.15) * mm, "end": v(-23.5, 8.55) * mm});
            skLineSegment(sketch, "E19.14.2", {"start": v(-9.4, 3.42) * mm, "end": v(-23.5, 8.55) * mm});
            skArc(sketch, "E19.14.3", {"start": v(-9.4, 3.42) * mm, "mid": v(-8.95, 4.46) * mm, "end": v(-8.39, 5.45) * mm});
            skSolve(sketch);
        }
        {
            var Q0;
            Q0 = qSketchRegion(id + "F2", true);
            var Q1;
            Q1=makeQuery(id+"F1.opRevolve","SWEPT_BODY",BODY,{"disambiguationData":[OSD([sQuery(id+"F0.wireOp",EDGE,"E0"),sQuery(id+"F0.wireOp",EDGE,"E1"),sQuery(id+"F0.wireOp",EDGE,"E2"),sQuery(id+"F0.wireOp",EDGE,"E3"),sQuery(id+"F0.wireOp",EDGE,"E4"),sQuery(id+"F0.wireOp",EDGE,"E5"),sQuery(id+"F0.wireOp",EDGE,"E6")])]});
            extrude(context, id + "F3", {"entities" : qUnion([Q0]), "operationType" : NewBodyOperationType.REMOVE, "oppositeDirection" : true, "depth" : 25 * mm, "endBoundEntityBody" : qUnion([Q1]), "offsetDistance" : 25 * mm, "hasSecondDirection" : true, "secondDirectionOppositeDirection" : false, "secondDirectionDepth" : 26.4 * mm});
        }
        {
            var Q0;
            Q0=makeQuery(id+"F1.opRevolve","SWEPT_FACE",FACE,{"disambiguationData":[OSD([sQuery(id+"F0.wireOp",EDGE,"E0")])]});
            var sketch = newSketch(context, id + "F4", { "sketchPlane" : qUnion([Q0])});
            skCircle(sketch, "E20", {"center": v(0, -83.65) * mm, "radius": 2.5 * mm});
            skCircle(sketch, "E21.1.0", {"center": v(25.85, -79.55) * mm, "radius": 2.5 * mm});
            skCircle(sketch, "E21.2.0", {"center": v(49.17, -67.67) * mm, "radius": 2.5 * mm});
            skCircle(sketch, "E21.3.0", {"center": v(67.67, -49.17) * mm, "radius": 2.5 * mm});
            skCircle(sketch, "E21.4.0", {"center": v(79.55, -25.85) * mm, "radius": 2.5 * mm});
            skCircle(sketch, "E21.5.0", {"center": v(83.65, 0) * mm, "radius": 2.5 * mm});
            skCircle(sketch, "E21.6.0", {"center": v(79.55, 25.85) * mm, "radius": 2.5 * mm});
            skCircle(sketch, "E21.7.0", {"center": v(67.67, 49.17) * mm, "radius": 2.5 * mm});
            skCircle(sketch, "E21.8.0", {"center": v(49.17, 67.67) * mm, "radius": 2.5 * mm});
            skCircle(sketch, "E21.9.0", {"center": v(25.85, 79.55) * mm, "radius": 2.5 * mm});
            skCircle(sketch, "E21.10.0", {"center": v(0, 83.65) * mm, "radius": 2.5 * mm});
            skCircle(sketch, "E21.11.0", {"center": v(-25.85, 79.55) * mm, "radius": 2.5 * mm});
            skCircle(sketch, "E21.12.0", {"center": v(-49.17, 67.67) * mm, "radius": 2.5 * mm});
            skCircle(sketch, "E21.13.0", {"center": v(-67.67, 49.17) * mm, "radius": 2.5 * mm});
            skCircle(sketch, "E21.14.0", {"center": v(-79.55, 25.85) * mm, "radius": 2.5 * mm});
            skCircle(sketch, "E21.15.0", {"center": v(-83.65, 0) * mm, "radius": 2.5 * mm});
            skCircle(sketch, "E21.16.0", {"center": v(-79.55, -25.85) * mm, "radius": 2.5 * mm});
            skCircle(sketch, "E21.17.0", {"center": v(-67.67, -49.17) * mm, "radius": 2.5 * mm});
            skCircle(sketch, "E21.18.0", {"center": v(-49.17, -67.67) * mm, "radius": 2.5 * mm});
            skCircle(sketch, "E21.19.0", {"center": v(-25.85, -79.55) * mm, "radius": 2.5 * mm});
            skPoint(sketch, "E21.center", {"position": v(0, 0) * mm});
            skSolve(sketch);
        }
        {
            var Q0;
            Q0 = qSketchRegion(id + "F4", true);
            extrude(context, id + "F5", {"entities" : qUnion([Q0]), "operationType" : NewBodyOperationType.REMOVE, "oppositeDirection" : true, "depth" : 2 * mm, "offsetDistance" : 25 * mm});
        }
        {
            var Q0;
            Q0=makeQuery(id+"F3.boolean.opBoolean","INTERSECT",EDGE,{"derivedFrom":[makeQuery(id+"F3.opExtrude","SWEPT_FACE",FACE,{"disambiguationData":[OSD([sQuery(id+"F2.wireOp",EDGE,"E8")])]}),makeQuery(id+"F3.opExtrude","SWEPT_FACE",FACE,{"disambiguationData":[OSD([sQuery(id+"F2.wireOp",EDGE,"E12.1.2")])]}),makeQuery(id+"F3.opExtrude","SWEPT_FACE",FACE,{"disambiguationData":[OSD([sQuery(id+"F2.wireOp",EDGE,"E12.2.2")])]}),makeQuery(id+"F3.opExtrude","SWEPT_FACE",FACE,{"disambiguationData":[OSD([sQuery(id+"F2.wireOp",EDGE,"E12.3.2")])]}),makeQuery(id+"F3.opExtrude","SWEPT_FACE",FACE,{"disambiguationData":[OSD([sQuery(id+"F2.wireOp",EDGE,"E12.4.2")])]}),makeQuery(id+"F3.opExtrude","SWEPT_FACE",FACE,{"disambiguationData":[OSD([sQuery(id+"F2.wireOp",EDGE,"E12.5.2")])]}),makeQuery(id+"F3.opExtrude","SWEPT_FACE",FACE,{"disambiguationData":[OSD([sQuery(id+"F2.wireOp",EDGE,"E12.6.2")])]}),makeQuery(id+"F3.opExtrude","SWEPT_FACE",FACE,{"disambiguationData":[OSD([sQuery(id+"F2.wireOp",EDGE,"E12.7.2")])]}),makeQuery(id+"F3.opExtrude","SWEPT_FACE",FACE,{"disambiguationData":[OSD([sQuery(id+"F2.wireOp",EDGE,"E12.8.2")])]}),makeQuery(id+"F3.opExtrude","SWEPT_FACE",FACE,{"disambiguationData":[OSD([sQuery(id+"F2.wireOp",EDGE,"E12.9.2")])]}),makeQuery(id+"F3.opExtrude","SWEPT_FACE",FACE,{"disambiguationData":[OSD([sQuery(id+"F2.wireOp",EDGE,"E12.10.2")])]}),makeQuery(id+"F3.opExtrude","SWEPT_FACE",FACE,{"disambiguationData":[OSD([sQuery(id+"F2.wireOp",EDGE,"E12.11.2")])]}),makeQuery(id+"F3.opExtrude","SWEPT_FACE",FACE,{"disambiguationData":[OSD([sQuery(id+"F2.wireOp",EDGE,"E12.12.2")])]}),makeQuery(id+"F3.opExtrude","SWEPT_FACE",FACE,{"disambiguationData":[OSD([sQuery(id+"F2.wireOp",EDGE,"E12.13.2")])]}),makeQuery(id+"F3.opExtrude","SWEPT_FACE",FACE,{"disambiguationData":[OSD([sQuery(id+"F2.wireOp",EDGE,"E12.14.2")])]}),makeQuery(id+"F3.opExtrude","SWEPT_FACE",FACE,{"disambiguationData":[OSD([sQuery(id+"F2.wireOp",EDGE,"E12.15.2")])]}),makeQuery(id+"F3.opExtrude","SWEPT_FACE",FACE,{"disambiguationData":[OSD([sQuery(id+"F2.wireOp",EDGE,"E12.16.2")])]}),makeQuery(id+"F3.opExtrude","SWEPT_FACE",FACE,{"disambiguationData":[OSD([sQuery(id+"F2.wireOp",EDGE,"E12.17.2")])]}),makeQuery(id+"F3.opExtrude","SWEPT_FACE",FACE,{"disambiguationData":[OSD([sQuery(id+"F2.wireOp",EDGE,"E12.18.2")])]}),makeQuery(id+"F3.opExtrude","SWEPT_FACE",FACE,{"disambiguationData":[OSD([sQuery(id+"F2.wireOp",EDGE,"E12.19.2")])]}),makeQuery(id+"F3.opExtrude","SWEPT_FACE",FACE,{"disambiguationData":[OSD([sQuery(id+"F2.wireOp",EDGE,"E12.20.2")])]}),makeQuery(id+"F3.opExtrude","SWEPT_FACE",FACE,{"disambiguationData":[OSD([sQuery(id+"F2.wireOp",EDGE,"E12.21.2")])]}),makeQuery(id+"F3.opExtrude","SWEPT_FACE",FACE,{"disambiguationData":[OSD([sQuery(id+"F2.wireOp",EDGE,"E12.22.2")])]}),makeQuery(id+"F3.opExtrude","SWEPT_FACE",FACE,{"disambiguationData":[OSD([sQuery(id+"F2.wireOp",EDGE,"E12.23.2")])]}),makeQuery(id+"F3.opExtrude","SWEPT_FACE",FACE,{"disambiguationData":[OSD([sQuery(id+"F2.wireOp",EDGE,"E12.24.2")])]}),makeQuery(id+"F3.opExtrude","SWEPT_FACE",FACE,{"disambiguationData":[OSD([sQuery(id+"F2.wireOp",EDGE,"E12.25.2")])]}),makeQuery(id+"F3.opExtrude","SWEPT_FACE",FACE,{"disambiguationData":[OSD([sQuery(id+"F2.wireOp",EDGE,"E12.26.2")])]}),makeQuery(id+"F3.opExtrude","SWEPT_FACE",FACE,{"disambiguationData":[OSD([sQuery(id+"F2.wireOp",EDGE,"E12.27.2")])]}),makeQuery(id+"F3.opExtrude","SWEPT_FACE",FACE,{"disambiguationData":[OSD([sQuery(id+"F2.wireOp",EDGE,"E12.28.2")])]}),makeQuery(id+"F3.opExtrude","SWEPT_FACE",FACE,{"disambiguationData":[OSD([sQuery(id+"F2.wireOp",EDGE,"E12.29.2")])]}),makeQuery(id+"F3.opExtrude","SWEPT_FACE",FACE,{"disambiguationData":[OSD([sQuery(id+"F2.wireOp",EDGE,"E13.6.30.0")])]}),makeQuery(id+"F3.opExtrude","SWEPT_FACE",FACE,{"disambiguationData":[OSD([sQuery(id+"F2.wireOp",EDGE,"E13.6.31.0")])]}),makeQuery(id+"F3.opExtrude","SWEPT_FACE",FACE,{"disambiguationData":[OSD([sQuery(id+"F2.wireOp",EDGE,"E13.6.32.0")])]}),makeQuery(id+"F3.opExtrude","SWEPT_FACE",FACE,{"disambiguationData":[OSD([sQuery(id+"F2.wireOp",EDGE,"E13.6.33.0")])]}),makeQuery(id+"F3.opExtrude","SWEPT_FACE",FACE,{"disambiguationData":[OSD([sQuery(id+"F2.wireOp",EDGE,"E13.6.34.0")])]}),makeQuery(id+"F3.opExtrude","SWEPT_FACE",FACE,{"disambiguationData":[OSD([sQuery(id+"F2.wireOp",EDGE,"E13.6.35.0")])]}),makeQuery(id+"F3.opExtrude","SWEPT_FACE",FACE,{"disambiguationData":[OSD([sQuery(id+"F2.wireOp",EDGE,"E13.6.36.0")])]}),makeQuery(id+"F3.opExtrude","SWEPT_FACE",FACE,{"disambiguationData":[OSD([sQuery(id+"F2.wireOp",EDGE,"E13.6.37.0")])]}),makeQuery(id+"F3.opExtrude","SWEPT_FACE",FACE,{"disambiguationData":[OSD([sQuery(id+"F2.wireOp",EDGE,"E13.6.38.0")])]}),makeQuery(id+"F3.opExtrude","SWEPT_FACE",FACE,{"disambiguationData":[OSD([sQuery(id+"F2.wireOp",EDGE,"E13.6.39.0")])]}),makeQuery(id+"F3.opExtrude","SWEPT_FACE",FACE,{"disambiguationData":[OSD([sQuery(id+"F2.wireOp",EDGE,"E13.6.40.0")])]}),makeQuery(id+"F3.opExtrude","SWEPT_FACE",FACE,{"disambiguationData":[OSD([sQuery(id+"F2.wireOp",EDGE,"E13.6.41.0")])]}),makeQuery(id+"F3.opExtrude","SWEPT_FACE",FACE,{"disambiguationData":[OSD([sQuery(id+"F2.wireOp",EDGE,"E13.6.42.0")])]}),makeQuery(id+"F3.opExtrude","SWEPT_FACE",FACE,{"disambiguationData":[OSD([sQuery(id+"F2.wireOp",EDGE,"E13.6.43.0")])]}),makeQuery(id+"F3.opExtrude","SWEPT_FACE",FACE,{"disambiguationData":[OSD([sQuery(id+"F2.wireOp",EDGE,"E13.6.44.0")])]})]});
            chamfer(context, id + "F6", {"entities" : qUnion([Q0]), "chamferType" : ChamferType.TWO_OFFSETS, "width1" : 3 * mm, "oppositeDirection" : false, "width2" : 6 * mm, "tangentPropagation" : true});
        }
    });
